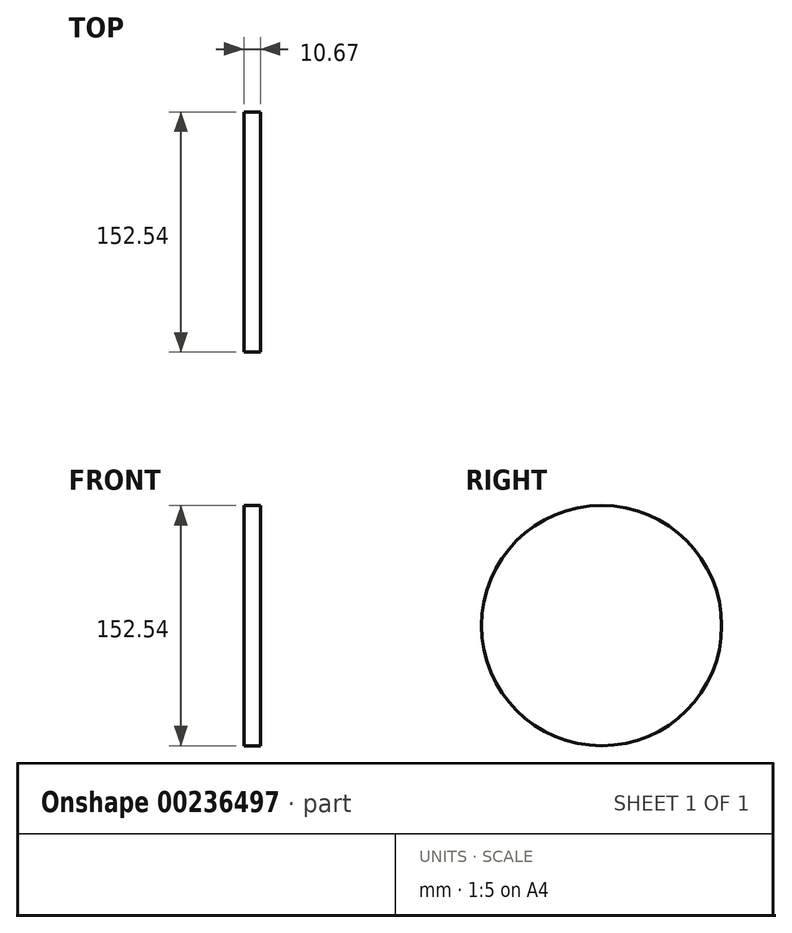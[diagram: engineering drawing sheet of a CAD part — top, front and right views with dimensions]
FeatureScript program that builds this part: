
annotation { "Feature Type Name" : "Feature", "Feature Type Description" : "" }
export const myFeature = defineFeature(function(context is Context, id is Id, definition is map)
    precondition{}
    {
        {
            var Q0;
            Q0=qCreatedBy(makeId("Right.planeOp"),FACE);
            var sketch = newSketch(context, id + "F0", { "sketchPlane" : qUnion([Q0])});
            skCircle(sketch, "E0", {"center": v(0, 0) * mm, "radius": 76.27 * mm});
            skSolve(sketch);
        }
        {
            var Q0;
            Q0=makeQuery(id+"F0.imprint","IMPRINT",FACE,{"disambiguationData":[TD([[makeQuery(id+"F0.imprint","IMPRINT",EDGE,{"derivedFrom":sQuery(id+"F0.wireOp",EDGE,"E0")}),1.0]])]});
            extrude(context, id + "F1", {"entities" : qUnion([Q0]), "depth" : 10.67 * mm});
        }
    });
